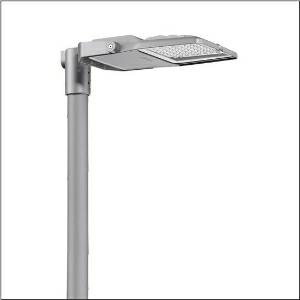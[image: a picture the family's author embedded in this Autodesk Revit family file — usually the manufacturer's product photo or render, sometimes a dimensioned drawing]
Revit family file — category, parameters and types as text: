
# Revit family: floodlight_fl_21_iq_mini___pl43_5xa7772b2a3a_a256
name_source: partatom
category: Lighting Fixtures
units: mm (PartAtom-declared; Revit-internal decimal feet)

## family parameters
Cut with Voids When Loaded = No
Host = Face
Light Source = No
Part Type = Normal
Room Calculation Point = No
Round Connector Dimension = Use Diameter
Shared = No

## types (1)
- --- (1 x LED, 6400 lm, 45.5 W, 3000K)
    Apparent Load = 46 VA
    CIE Flux Codes = 27 78 99 100 100
    Color Rendering = 70
    Color Temperature = 3000K
    Default Elevation = 1800 mm
    Description = Floodlight FL 21 iQ mini, floodlight, primary light control with lens, of PMMA, primary optical cover: protective disc, of toughened safety glass, transparent, light distribution: PL43, light emission: direct distribution, installation type: surface-mounted, LED, High Power LED, rated luminous flux: 6.400lm, luminous efficacy: 141lm/W, light colour: 730, colour temperature: 3000K, control gear: iQ Street-Remote/DALI, control: Auto-Match, Temp-Guard, Night-Set, Smart-Wire, Desk-Remote (wireless, voltage-free reading and setting of iQ features in the workshop via application-optimized NFC function/RFID function), optimised constant luminous flux control (CLO 2.0), Light-Fading, Lumen-Switch, with terminal, 6-pole, mains connection: 220..240V, AC, 50/60Hz, start of lifetime: 46W, end of service life: 48W, reduction: 22W, luminaire housing, of diecast aluminium, powder-coated, Siteco® metallic grey (DB 702S), corrosivity category C5 mid according to DIN EN ISO 12944, suitable for swimming pools, chlorine-resistant, sealing non-destructively replaceable, please order mast flange separately, mast bracket, of steel, galvanised, powder-coated, protection rating (complete): IP66, insulation class (complete): insulation class II (safety insulation), certification: CE, ENEC, VDE, protection symbol: D, impact resistance: IK08, permissible operating ambient temperature: -40..+40°C, permissible operating ambient temperature for outdoor applications: -40..+50°C, standard: DIN EN 12944, LABS conformity tested according to VDMA 24364:2018-05, packaging unit: 1 piece

Light Distribution: PL43
    Height = 70 mm
    Lamp = 1 x LED
    Lamp Light Flux = 6400 lm
    Lamp Power = 45.5 W
    Lamp count = 1
    Length = 485 mm
    Luminous efficacy = 141 lm/W
    Manufacturer = Siteco
    ModVariant = No
    Model = 5XA7772B2A3A
    Number of Poles = 1
    OnlyDefault = Yes
    Power Factor = 1
    Product Name = Floodlight FL 21 iQ mini | PL43
    Product group = floodlight | pylon annexe
    ProductGroupID = 6201
    Protection Class = Protection class II
    Protection Degree = IP 66
    RLX_Detail_Level = 1
    RLX_Emergency_Light_Flux = 0 lm
    RLX_Emergency_Type = 0
    RLX_Emergency_Type_DB = No
    RlxData = <blob elided: 101281 chars, md5=8abfd40b>
    Socket = socket
    Standby Power = 0 W
    System Light Flux = 6400 lm
    System Power = 46 W
    Type Comments = factory setting: luminous flux: 100 % | dim-lin: 254 | 463 mA
    Type Image = l_1007125.jpg
    URL = http://relux.com
    VarID = @adj_184239
    Voltage = 0 V
    Weight = 0.00 kg
    Width = 337 mm

## geometry (parser evidence)
native form markers: Blend x4, Sweep x15
no freeform markers — native parametric forms only
